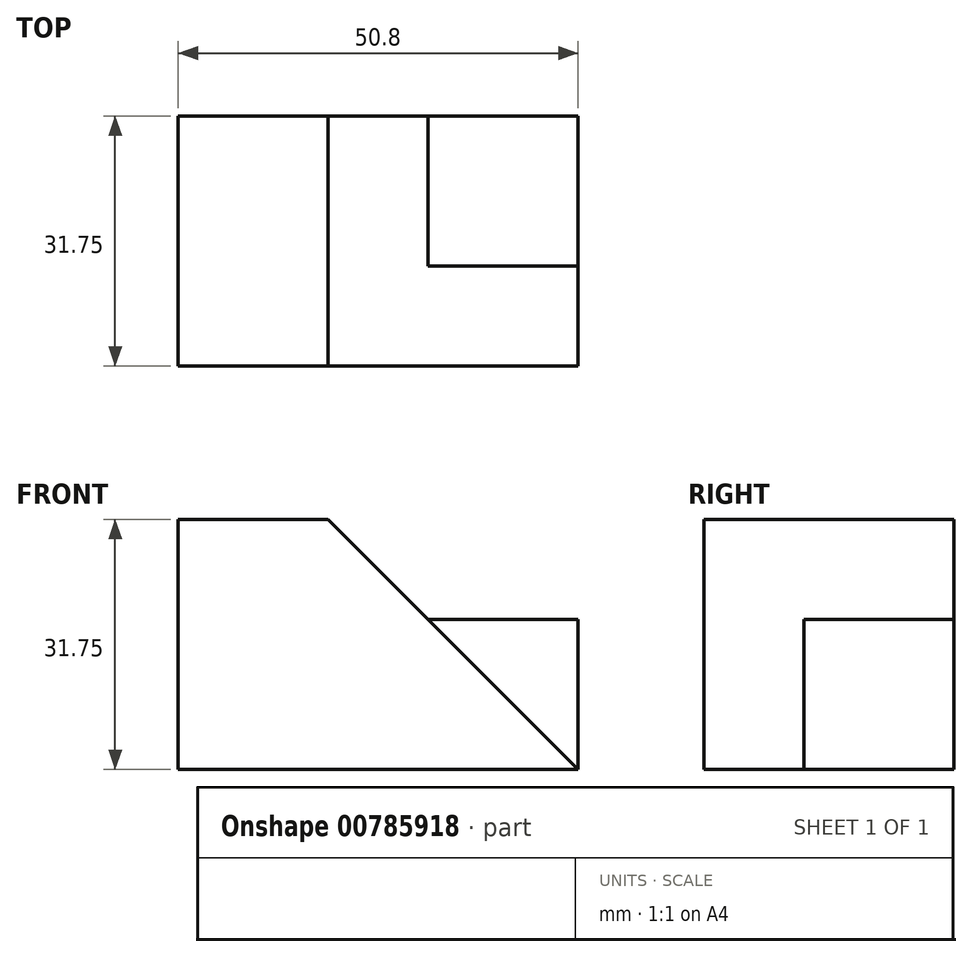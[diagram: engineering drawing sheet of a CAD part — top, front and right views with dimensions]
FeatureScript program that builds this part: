
annotation { "Feature Type Name" : "Feature", "Feature Type Description" : "" }
export const myFeature = defineFeature(function(context is Context, id is Id, definition is map)
    precondition{}
    {
        {
            var Q0;
            Q0=qCreatedBy(makeId("Front.planeOp"),FACE);
            var sketch = newSketch(context, id + "F0", { "sketchPlane" : qUnion([Q0])});
            skLineSegment(sketch, "E0", {"start": v(0, 0) * mm, "end": v(50.8, 0) * mm});
            skLineSegment(sketch, "E1", {"start": v(0, 0) * mm, "end": v(0, 31.75) * mm});
            skLineSegment(sketch, "E2", {"start": v(0, 31.75) * mm, "end": v(50.8, 31.75) * mm});
            skLineSegment(sketch, "E3", {"start": v(50.8, 31.75) * mm, "end": v(50.8, 0) * mm});
            skSolve(sketch);
        }
        {
            var Q0;
            Q0=makeQuery(id+"F0.imprint","IMPRINT",FACE,{"disambiguationData":[TD([[makeQuery(id+"F0.imprint","IMPRINT",EDGE,{"derivedFrom":sQuery(id+"F0.wireOp",EDGE,"E0")}),1.0]])]});
            extrude(context, id + "F1", {"entities" : qUnion([Q0]), "depth" : 31.75 * mm, "offsetDistance" : 25.4 * mm});
        }
        {
            var Q0;
            Q0=makeQuery(id+"F1.opExtrude","CAP_FACE",FACE,{"disambiguationData":[OSD([sQuery(id+"F0.wireOp",EDGE,"E0"),sQuery(id+"F0.wireOp",EDGE,"E1"),sQuery(id+"F0.wireOp",EDGE,"E2"),sQuery(id+"F0.wireOp",EDGE,"E3")])],"isStart":false});
            var sketch = newSketch(context, id + "F2", { "sketchPlane" : qUnion([Q0])});
            skLineSegment(sketch, "E4", {"start": v(0, 31.75) * mm, "end": v(19.05, 31.75) * mm});
            skLineSegment(sketch, "E5", {"start": v(19.05, 31.75) * mm, "end": v(50.8, 0) * mm});
            skLineSegment(sketch, "E6", {"start": v(0, 0) * mm, "end": v(50.8, 0) * mm});
            skLineSegment(sketch, "E7", {"start": v(0, 31.75) * mm, "end": v(0, 0) * mm});
            skLineSegment(sketch, "E8", {"start": v(19.05, 31.75) * mm, "end": v(50.8, 31.75) * mm});
            skLineSegment(sketch, "E9", {"start": v(50.8, 31.75) * mm, "end": v(50.8, 0) * mm});
            skSolve(sketch);
        }
        {
            var Q0;
            Q0=makeQuery(id+"F1.opExtrude","SWEPT_FACE",FACE,{"disambiguationData":[OSD([sQuery(id+"F0.wireOp",EDGE,"E3")])]});
            var sketch = newSketch(context, id + "F3", { "sketchPlane" : qUnion([Q0])});
            skLineSegment(sketch, "E10", {"start": v(0, 0) * mm, "end": v(-19.05, 0) * mm});
            skLineSegment(sketch, "E11", {"start": v(-19.05, 0) * mm, "end": v(-19.05, 19.05) * mm});
            skLineSegment(sketch, "E12", {"start": v(-19.05, 19.05) * mm, "end": v(0, 19.05) * mm});
            skLineSegment(sketch, "E13", {"start": v(0, 19.05) * mm, "end": v(0, 0) * mm});
            skSolve(sketch);
        }
        {
            var Q0;
            Q0=makeQuery(id+"F2.imprint","IMPRINT",FACE,{"disambiguationData":[TD([[makeQuery(id+"F2.imprint","IMPRINT",EDGE,{"derivedFrom":sQuery(id+"F2.wireOp",EDGE,"E5")}),1.0]])]});
            extrude(context, id + "F4", {"entities" : qUnion([Q0]), "operationType" : NewBodyOperationType.REMOVE, "oppositeDirection" : true, "depth" : 12.7 * mm, "offsetDistance" : 25.4 * mm});
        }
        {
            var Q0;
            Q0=makeQuery(id+"F1.opExtrude","CAP_FACE",FACE,{"disambiguationData":[OSD([sQuery(id+"F0.wireOp",EDGE,"E0"),sQuery(id+"F0.wireOp",EDGE,"E1"),sQuery(id+"F0.wireOp",EDGE,"E2"),sQuery(id+"F0.wireOp",EDGE,"E3")])],"isStart":true});
            var sketch = newSketch(context, id + "F5", { "sketchPlane" : qUnion([Q0])});
            skLineSegment(sketch, "E14", {"start": v(-50.8, 31.75) * mm, "end": v(-50.8, 19.05) * mm});
            skLineSegment(sketch, "E15", {"start": v(-50.8, 19.05) * mm, "end": v(-31.75, 19.05) * mm});
            skLineSegment(sketch, "E16", {"start": v(0, 31.75) * mm, "end": v(-19.05, 31.75) * mm});
            skLineSegment(sketch, "E17", {"start": v(-31.75, 19.05) * mm, "end": v(-19.05, 31.75) * mm});
            skSolve(sketch);
        }
        {
            var Q0;
            {var subQ0=sQuery(id+"F5.wireOp",EDGE,"E14");Q0=makeQuery(id+"F5.imprint","IMPRINT",FACE,{"disambiguationData":[TD([[makeQuery(id+"F5.imprint","IMPRINT",EDGE,{"derivedFrom":subQ0}),1.0]])]});}
            extrude(context, id + "F6", {"entities" : qUnion([Q0]), "operationType" : NewBodyOperationType.REMOVE, "oppositeDirection" : true, "depth" : 25.4 * mm, "offsetDistance" : 25.4 * mm});
        }
    });
